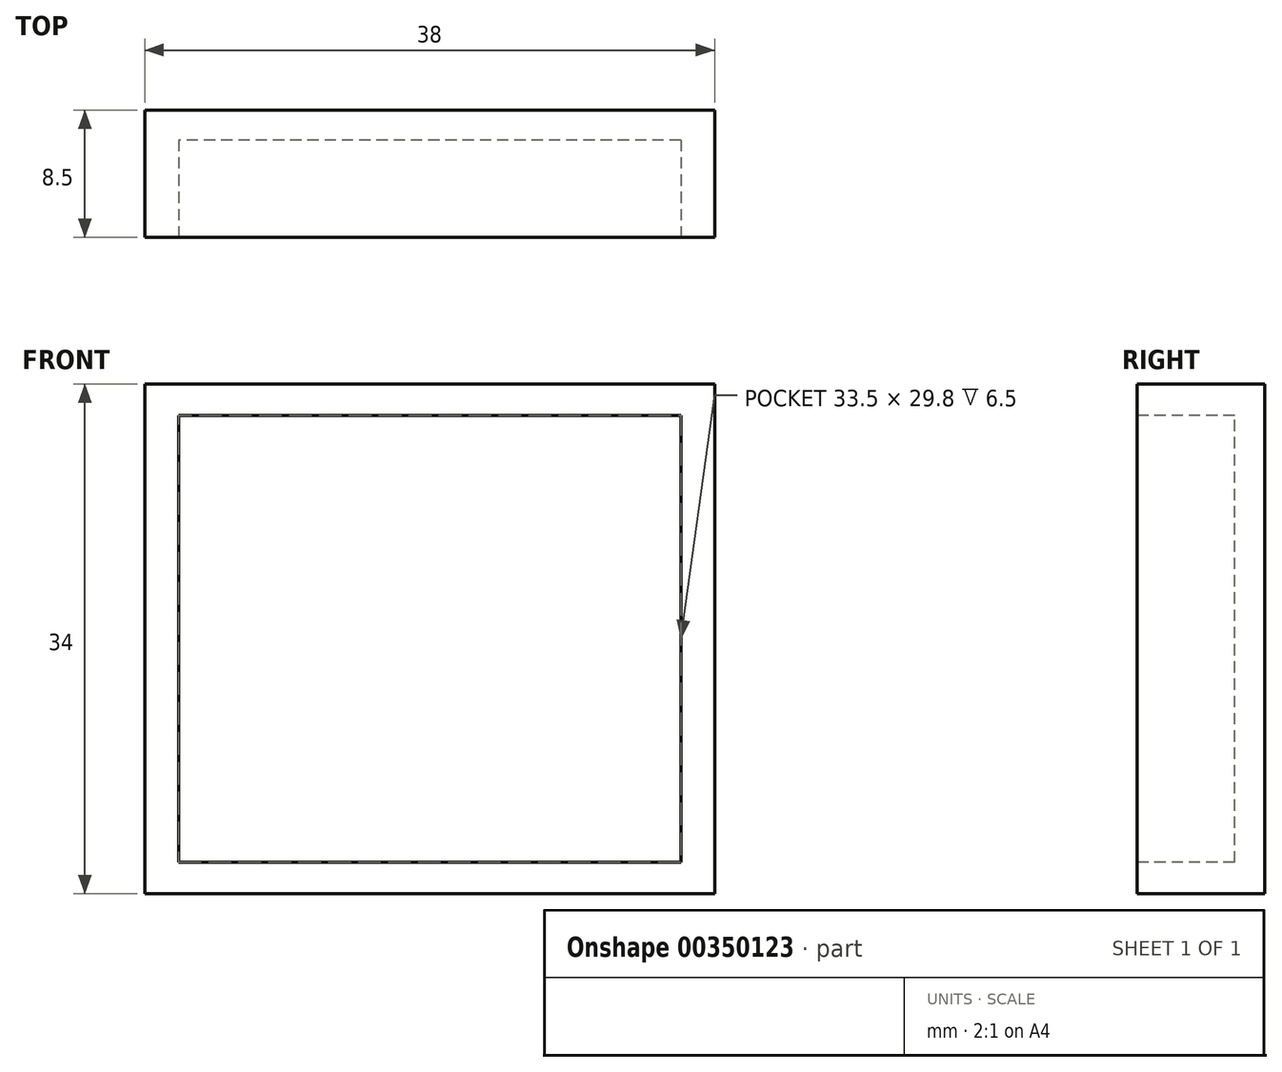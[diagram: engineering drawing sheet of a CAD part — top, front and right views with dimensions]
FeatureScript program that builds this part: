
annotation { "Feature Type Name" : "Feature", "Feature Type Description" : "" }
export const myFeature = defineFeature(function(context is Context, id is Id, definition is map)
    precondition{}
    {
        {
            var Q0;
            Q0=qCreatedBy(makeId("Front.planeOp"),FACE);
            var sketch = newSketch(context, id + "F0", { "sketchPlane" : qUnion([Q0])});
            skLineSegment(sketch, "E0.bottom", {"start": v(19, -17) * mm, "end": v(-19, -17) * mm});
            skLineSegment(sketch, "E0.top", {"start": v(19, 17) * mm, "end": v(-19, 17) * mm});
            skLineSegment(sketch, "E0.left", {"start": v(19, -17) * mm, "end": v(19, 17) * mm});
            skLineSegment(sketch, "E0.right", {"start": v(-19, -17) * mm, "end": v(-19, 17) * mm});
            skPoint(sketch, "E0.middle", {"position": v(0, 0) * mm});
            skSolve(sketch);
        }
        {
            var Q0;
            Q0=makeQuery(id+"F0.imprint","IMPRINT",FACE,{"disambiguationData":[TD([[makeQuery(id+"F0.imprint","IMPRINT",EDGE,{"derivedFrom":sQuery(id+"F0.wireOp",EDGE,"E0.bottom")}),-1.0]])]});
            extrude(context, id + "F1", {"entities" : qUnion([Q0]), "depth" : 8.5 * mm});
        }
        {
            var Q0;
            Q0=makeQuery(id+"F1.opExtrude","CAP_FACE",FACE,{"disambiguationData":[OSD([sQuery(id+"F0.wireOp",EDGE,"E0.bottom"),sQuery(id+"F0.wireOp",EDGE,"E0.top"),sQuery(id+"F0.wireOp",EDGE,"E0.left"),sQuery(id+"F0.wireOp",EDGE,"E0.right")])],"isStart":false});
            var sketch = newSketch(context, id + "F2", { "sketchPlane" : qUnion([Q0])});
            skLineSegment(sketch, "E1.bottom", {"start": v(16.75, -14.9) * mm, "end": v(-16.75, -14.9) * mm});
            skLineSegment(sketch, "E1.top", {"start": v(16.75, 14.9) * mm, "end": v(-16.75, 14.9) * mm});
            skLineSegment(sketch, "E1.left", {"start": v(16.75, -14.9) * mm, "end": v(16.75, 14.9) * mm});
            skLineSegment(sketch, "E1.right", {"start": v(-16.75, -14.9) * mm, "end": v(-16.75, 14.9) * mm});
            skPoint(sketch, "E1.middle", {"position": v(0, 0) * mm});
            skPoint(sketch, "E2", {"position": v(-16.75, 14.9) * mm});
            skPoint(sketch, "E3", {"position": v(16.75, 14.9) * mm});
            skPoint(sketch, "E4", {"position": v(16.75, -14.9) * mm});
            skPoint(sketch, "E5", {"position": v(-16.75, -14.9) * mm});
            skSolve(sketch);
        }
        {
            var Q0;
            Q0=makeQuery(id+"F2.imprint","IMPRINT",FACE,{"disambiguationData":[TD([[makeQuery(id+"F2.imprint","IMPRINT",EDGE,{"derivedFrom":sQuery(id+"F2.wireOp",EDGE,"E1.bottom")}),-1.0]])]});
            extrude(context, id + "F3", {"entities" : qUnion([Q0]), "operationType" : NewBodyOperationType.REMOVE, "oppositeDirection" : true, "depth" : 6.5 * mm});
        }
    });
